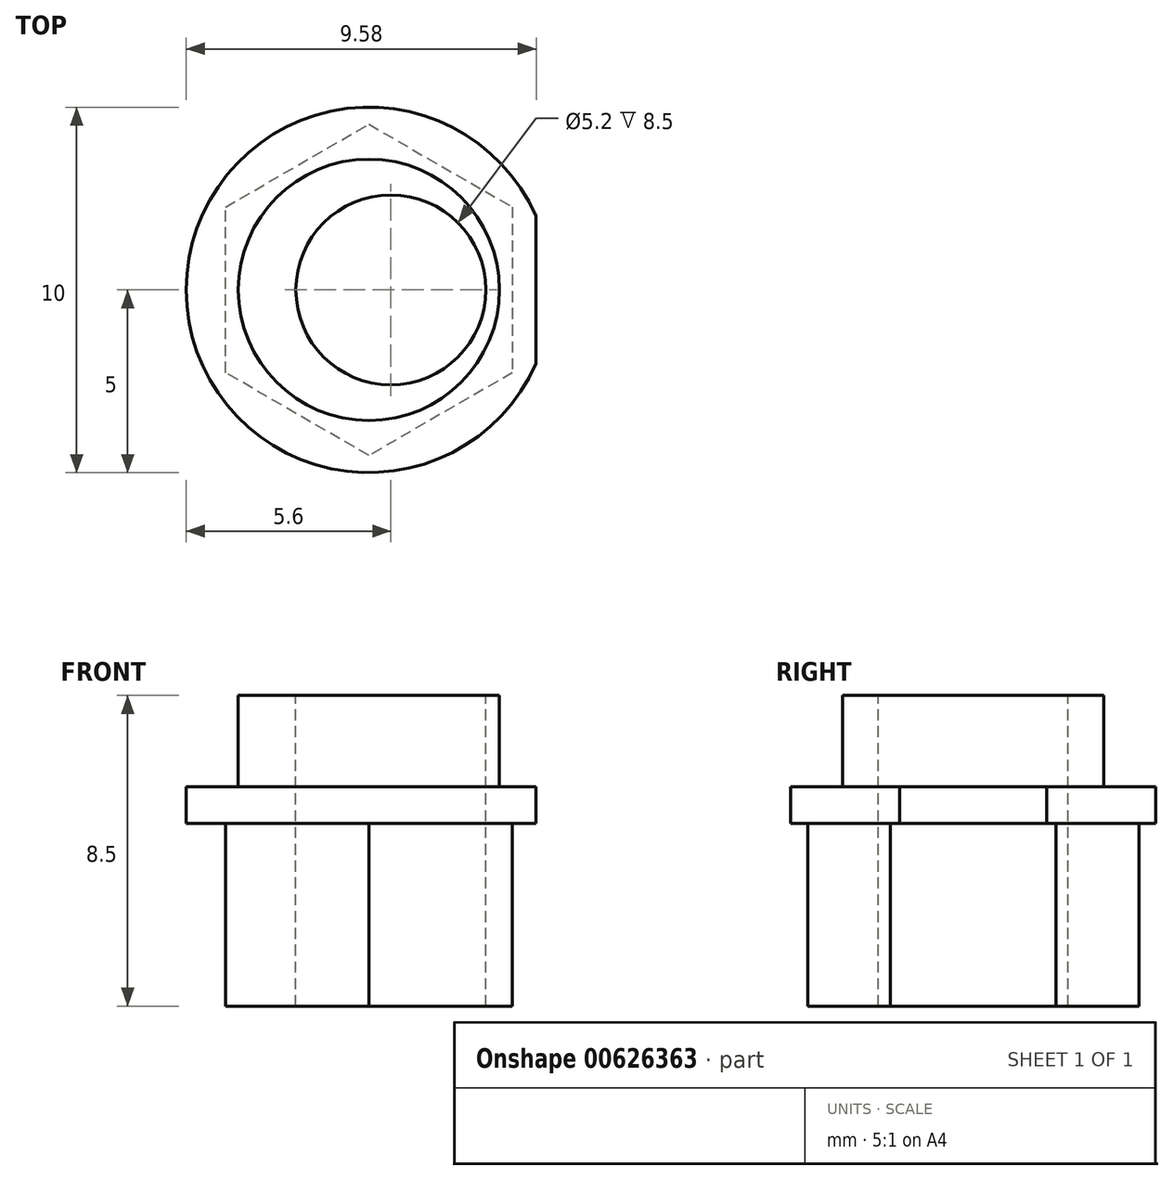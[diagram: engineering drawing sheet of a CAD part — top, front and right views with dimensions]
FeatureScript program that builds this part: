
annotation { "Feature Type Name" : "Feature", "Feature Type Description" : "" }
export const myFeature = defineFeature(function(context is Context, id is Id, definition is map)
    precondition{}
    {
        {
            var Q0;
            Q0=qCreatedBy(makeId("Top.planeOp"),FACE);
            var sketch = newSketch(context, id + "F0", { "sketchPlane" : qUnion([Q0])});
            skCircle(sketch, "E0.cCircle", {"center": v(0, 0) * mm, "radius": 3.92 * mm, "construction": true});
            skLineSegment(sketch, "E0.0", {"start": v(3.92, 2.27) * mm, "end": v(3.92, -2.27) * mm});
            skLineSegment(sketch, "E0.1", {"start": v(3.92, -2.27) * mm, "end": v(0, -4.53) * mm});
            skLineSegment(sketch, "E0.2", {"start": v(0, -4.53) * mm, "end": v(-3.92, -2.27) * mm});
            skLineSegment(sketch, "E0.3", {"start": v(-3.92, -2.27) * mm, "end": v(-3.93, 2.27) * mm});
            skLineSegment(sketch, "E0.4", {"start": v(-3.93, 2.27) * mm, "end": v(0, 4.53) * mm});
            skLineSegment(sketch, "E0.5", {"start": v(0, 4.53) * mm, "end": v(3.93, 2.27) * mm});
            skPoint(sketch, "E0.0.midPoint", {"position": v(3.92, 0) * mm});
            skSolve(sketch);
        }
        {
            var Q0;
            Q0 = qSketchRegion(id + "F0", true);
            extrude(context, id + "F1", {"entities" : qUnion([Q0]), "depth" : 5 * mm, "offsetDistance" : 25 * mm});
        }
        {
            var Q0;
            Q0=makeQuery(id+"F1.opExtrude","CAP_FACE",FACE,{"disambiguationData":[OSD([sQuery(id+"F0.wireOp",EDGE,"E0.0"),sQuery(id+"F0.wireOp",EDGE,"E0.1"),sQuery(id+"F0.wireOp",EDGE,"E0.2"),sQuery(id+"F0.wireOp",EDGE,"E0.3"),sQuery(id+"F0.wireOp",EDGE,"E0.4"),sQuery(id+"F0.wireOp",EDGE,"E0.5")])],"isStart":false});
            var sketch = newSketch(context, id + "F2", { "sketchPlane" : qUnion([Q0])});
            skCircle(sketch, "E1", {"center": v(0, 0) * mm, "radius": 3.58 * mm});
            skSolve(sketch);
        }
        {
            var Q0;
            Q0 = qSketchRegion(id + "F2", true);
            extrude(context, id + "F3", {"entities" : qUnion([Q0]), "operationType" : NewBodyOperationType.ADD, "depth" : 3.5 * mm, "offsetDistance" : 25 * mm});
        }
        {
            var Q0;
            Q0=makeQuery(id+"F3.opExtrude","CAP_FACE",FACE,{"disambiguationData":[OSD([sQuery(id+"F2.wireOp",EDGE,"E1")])],"isStart":false});
            var sketch = newSketch(context, id + "F4", { "sketchPlane" : qUnion([Q0])});
            skCircle(sketch, "E2", {"center": v(0.6, 0) * mm, "radius": 2.6 * mm});
            skSolve(sketch);
        }
        {
            var Q0;
            Q0 = qSketchRegion(id + "F4", true);
            extrude(context, id + "F5", {"entities" : qUnion([Q0]), "operationType" : NewBodyOperationType.REMOVE, "oppositeDirection" : true, "depth" : 25 * mm, "offsetDistance" : 25 * mm});
        }
        {
            var Q0;
            Q0=makeQuery(id+"F1.opExtrude","CAP_FACE",FACE,{"disambiguationData":[OSD([sQuery(id+"F0.wireOp",EDGE,"E0.0"),sQuery(id+"F0.wireOp",EDGE,"E0.1"),sQuery(id+"F0.wireOp",EDGE,"E0.2"),sQuery(id+"F0.wireOp",EDGE,"E0.3"),sQuery(id+"F0.wireOp",EDGE,"E0.4"),sQuery(id+"F0.wireOp",EDGE,"E0.5")])],"isStart":false});
            var sketch = newSketch(context, id + "F6", { "sketchPlane" : qUnion([Q0])});
            skCircle(sketch, "E3", {"center": v(0, 0) * mm, "radius": 5 * mm});
            skSolve(sketch);
        }
        {
            var Q0;
            Q0 = qSketchRegion(id + "F6", true);
            extrude(context, id + "F7", {"entities" : qUnion([Q0]), "operationType" : NewBodyOperationType.ADD, "depth" : 1 * mm, "offsetDistance" : 25 * mm});
        }
        {
            var Q0;
            Q0=makeQuery(id+"F3.opExtrude","CAP_FACE",FACE,{"disambiguationData":[OSD([sQuery(id+"F2.wireOp",EDGE,"E1")])],"isStart":false});
            var sketch = newSketch(context, id + "F8", { "sketchPlane" : qUnion([Q0])});
            skCircle(sketch, "E4", {"center": v(0.6, 0) * mm, "radius": 2.6 * mm});
            skSolve(sketch);
        }
        {
            var Q0;
            Q0 = qSketchRegion(id + "F8", true);
            extrude(context, id + "F9", {"entities" : qUnion([Q0]), "operationType" : NewBodyOperationType.REMOVE, "oppositeDirection" : true, "depth" : 25 * mm, "offsetDistance" : 25 * mm});
        }
        {
            var Q0;
            {var subQ0=sQuery(id+"F6.wireOp",EDGE,"E3");Q0=makeQuery(id+"F7.boolean.opBoolean","SPLIT",FACE,{"disambiguationData":[TD([makeQuery(id+"F3.opExtrude","SWEPT_FACE",FACE,{"disambiguationData":[OSD([sQuery(id+"F2.wireOp",EDGE,"E1")])]})])],"derivedFrom":makeQuery(id+"F7.opExtrude","CAP_FACE",FACE,{"disambiguationData":[OSD([subQ0])],"isStart":false})});}
            var sketch = newSketch(context, id + "F10", { "sketchPlane" : qUnion([Q0])});
            skLineSegment(sketch, "E5.bottom", {"start": v(6.07, 2.5) * mm, "end": v(4.57, 2.5) * mm});
            skLineSegment(sketch, "E5.top", {"start": v(6.08, -2.5) * mm, "end": v(4.58, -2.5) * mm});
            skLineSegment(sketch, "E5.left", {"start": v(6.07, 2.5) * mm, "end": v(6.08, -2.5) * mm});
            skLineSegment(sketch, "E5.right", {"start": v(4.57, 2.5) * mm, "end": v(4.58, -2.5) * mm});
            skSolve(sketch);
        }
        {
            var Q0;
            Q0 = qSketchRegion(id + "F10", true);
            extrude(context, id + "F11", {"entities" : qUnion([Q0]), "operationType" : NewBodyOperationType.REMOVE, "oppositeDirection" : true, "depth" : 2 * mm, "offsetDistance" : 25 * mm});
        }
    });
